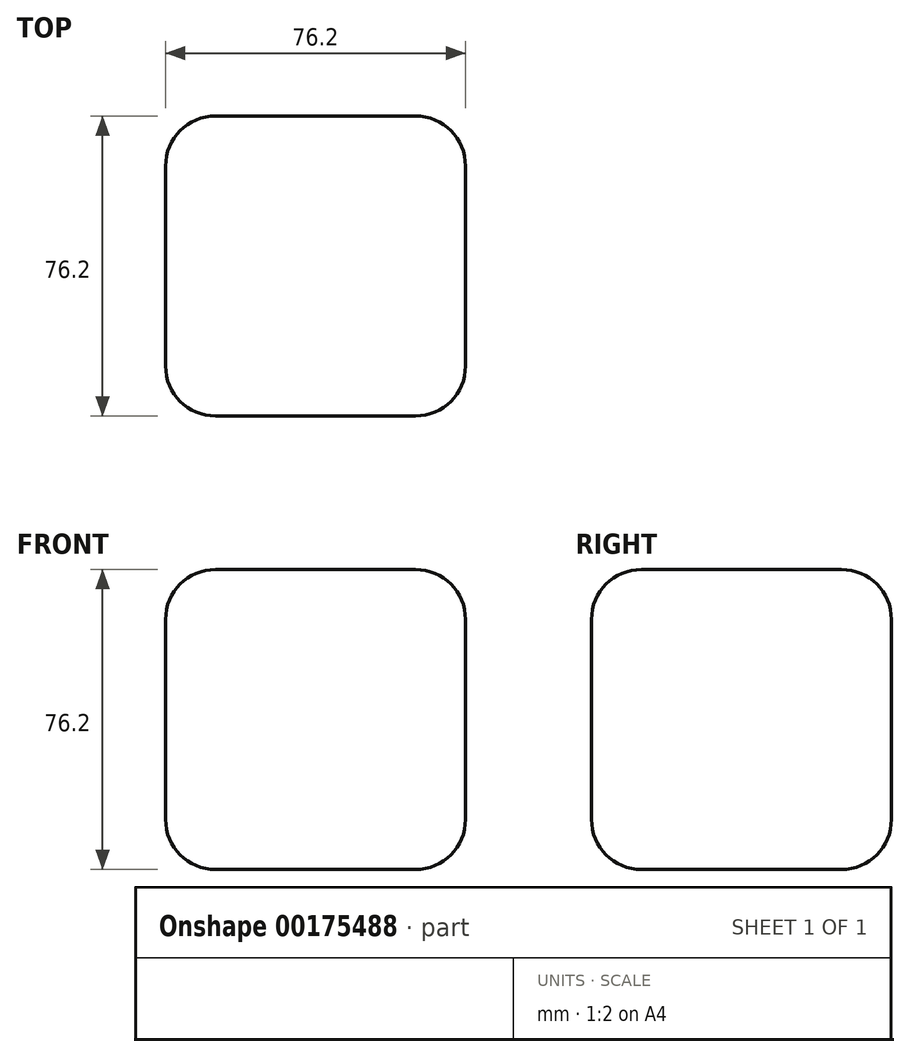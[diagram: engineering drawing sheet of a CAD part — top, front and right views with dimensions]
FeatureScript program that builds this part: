
annotation { "Feature Type Name" : "Feature", "Feature Type Description" : "" }
export const myFeature = defineFeature(function(context is Context, id is Id, definition is map)
    precondition{}
    {
        {
            var Q0;
            Q0=qCreatedBy(makeId("Top.planeOp"),FACE);
            var sketch = newSketch(context, id + "F0", { "sketchPlane" : qUnion([Q0])});
            skLineSegment(sketch, "E0.bottom", {"start": v(38.1, 38.1) * mm, "end": v(-38.1, 38.1) * mm});
            skLineSegment(sketch, "E0.top", {"start": v(38.1, -38.1) * mm, "end": v(-38.1, -38.1) * mm});
            skLineSegment(sketch, "E0.left", {"start": v(38.1, 38.1) * mm, "end": v(38.1, -38.1) * mm});
            skLineSegment(sketch, "E0.right", {"start": v(-38.1, 38.1) * mm, "end": v(-38.1, -38.1) * mm});
            skPoint(sketch, "E0.middle", {"position": v(0, 0) * mm});
            skSolve(sketch);
        }
        {
            var Q0;
            Q0=makeQuery(id+"F0.imprint","IMPRINT",FACE,{"disambiguationData":[TD([[makeQuery(id+"F0.imprint","IMPRINT",EDGE,{"derivedFrom":sQuery(id+"F0.wireOp",EDGE,"E0.bottom")}),1.0]])]});
            extrude(context, id + "F1", {"entities" : qUnion([Q0]), "endBound" : BoundingType.SYMMETRIC, "depth" : 76.2 * mm});
        }
        {
            var Q0;
            Q0=makeQuery(id+"F1.opExtrude","CAP_FACE",FACE,{"disambiguationData":[OSD([sQuery(id+"F0.wireOp",EDGE,"E0.bottom"),sQuery(id+"F0.wireOp",EDGE,"E0.top"),sQuery(id+"F0.wireOp",EDGE,"E0.left"),sQuery(id+"F0.wireOp",EDGE,"E0.right")])],"isStart":false});
            var Q1;
            Q1=makeQuery(id+"F1.opExtrude","SWEPT_EDGE",EDGE,{"disambiguationData":[OSD([sQuery(id+"F0.wireOp",EDGE,"E0.bottom"),sQuery(id+"F0.wireOp",EDGE,"E0.right")])]});
            var Q2;
            Q2=makeQuery(id+"F1.opExtrude","CAP_EDGE",EDGE,{"disambiguationData":[OSD([sQuery(id+"F0.wireOp",EDGE,"E0.bottom")])],"isStart":true});
            var Q3;
            Q3=makeQuery(id+"F1.opExtrude","SWEPT_EDGE",EDGE,{"disambiguationData":[OSD([sQuery(id+"F0.wireOp",EDGE,"E0.bottom"),sQuery(id+"F0.wireOp",EDGE,"E0.left")])]});
            var Q4;
            Q4=makeQuery(id+"F1.opExtrude","SWEPT_EDGE",EDGE,{"disambiguationData":[OSD([sQuery(id+"F0.wireOp",EDGE,"E0.top"),sQuery(id+"F0.wireOp",EDGE,"E0.left")])]});
            var Q5;
            Q5=makeQuery(id+"F1.opExtrude","CAP_FACE",FACE,{"disambiguationData":[OSD([sQuery(id+"F0.wireOp",EDGE,"E0.bottom"),sQuery(id+"F0.wireOp",EDGE,"E0.top"),sQuery(id+"F0.wireOp",EDGE,"E0.left"),sQuery(id+"F0.wireOp",EDGE,"E0.right")])],"isStart":true});
            var Q6;
            Q6=makeQuery(id+"F1.opExtrude","SWEPT_EDGE",EDGE,{"disambiguationData":[OSD([sQuery(id+"F0.wireOp",EDGE,"E0.top"),sQuery(id+"F0.wireOp",EDGE,"E0.right")])]});
            fillet(context, id + "F2", {"entities" : qUnion([Q0, Q1, Q2, Q3, Q4, Q5, Q6]), "radius" : 12.7 * mm, "tangentPropagation" : true, "allowEdgeOverflow" : false});
        }
    });
